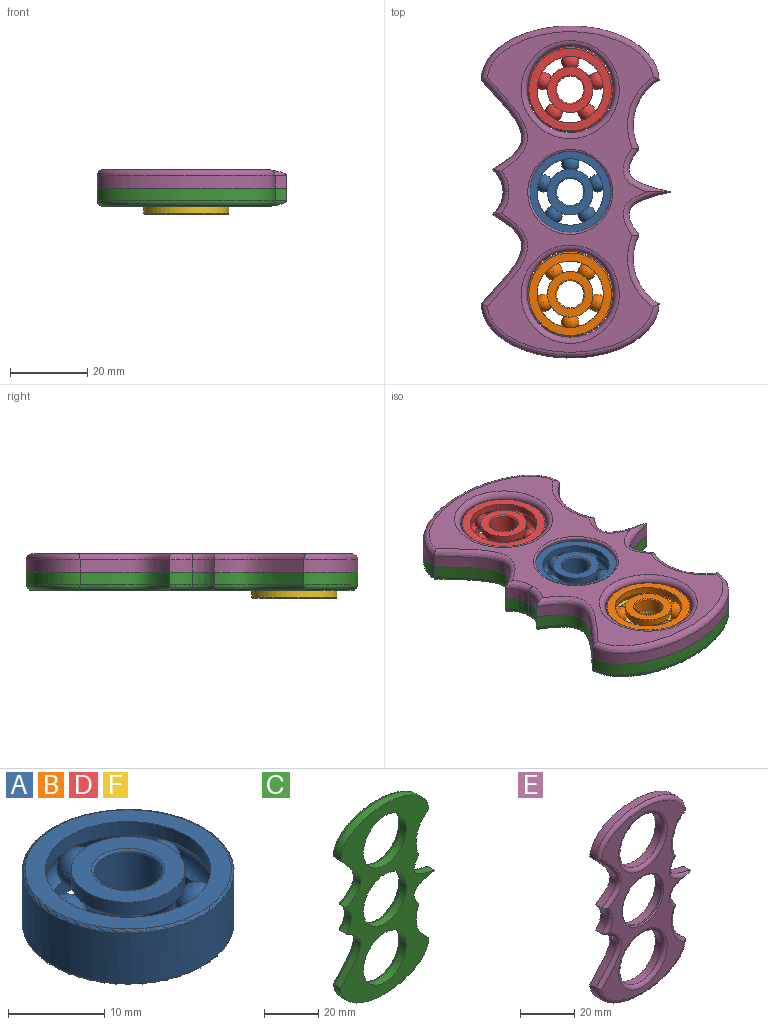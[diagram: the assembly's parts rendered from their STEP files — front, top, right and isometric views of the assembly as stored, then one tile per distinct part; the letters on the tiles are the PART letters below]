
ASSEMBLY  parts=6 mates=5
PART A: 29 faces, bbox 23.8x23.8x7 mm
  f0: torus R=3.8mm, axis (0,0,1), area 10.7mm2, adj f1,f2
  f1: cylinder r=3.5mm len=7mm, axis (0,0,1), area 140.7mm2, adj f0,f3
  f2: plane 11.8x11.8mm, normal (0,0,1), area 64mm2, adj f0,f14
  f3: torus R=3.8mm, axis (0,0,1), area 10.7mm2, adj f1,f4
  f4: plane 11.8x11.8mm, normal (0,0,-1), area 64mm2, adj f3,f25
  f5: torus R=10.7mm, axis (0,0,1), area 32.2mm2, adj f6,f7
  f6: cylinder r=11mm len=22mm, axis (0,0,1), area 442.3mm2, adj f5,f8
  f7: plane 21.4x21.4mm, normal (0,0,-1), area 127.3mm2, adj f5,f27
  f8: torus R=10.7mm, axis (0,0,1), area 32.2mm2, adj f6,f9
  f9: plane 21.4x21.4mm, normal (0,0,1), area 127.3mm2, adj f8,f19
  f10: sphere r=2.25mm, area 63.4mm2, adj f14,f15,f19,f23,f25,f26,f27,f28
  f11: sphere r=2.25mm, area 63.4mm2, adj f14,f18,f19,f22,f23,f25,f26,f27
  f12: sphere r=2.25mm, area 63.4mm2, adj f14,f17,f18,f19,f21,f22,f25,f27
  f13: sphere r=2.25mm, area 63.4mm2, adj f14,f16,f17,f19,f20,f21,f25,f27
  f14: cylinder r=5.9mm len=11.8mm, axis (0,0,1), area 63mm2, adj f2,f10,f11,f12,f13,f15,f16,f17
  f15: torus R=7.25mm, axis (0,0,1), area 27.7mm2, adj f10,f14,f24,f25
  f16: torus R=7.25mm, axis (0,0,1), area 27.7mm2, adj f13,f14,f24,f25
  f17: torus R=7.25mm, axis (0,0,1), area 27.7mm2, adj f12,f13,f14,f25
  f18: torus R=7.25mm, axis (0,0,1), area 27.7mm2, adj f11,f12,f14,f25
  f19: cylinder r=8.6mm len=17.2mm, axis (0,0,1), area 91.9mm2, adj f9,f10,f11,f12,f13,f20,f21,f22
  f20: torus R=7.25mm, axis (0,0,1), area 48.1mm2, adj f13,f19,f24,f27
  f21: torus R=7.25mm, axis (0,0,1), area 48.1mm2, adj f12,f13,f19,f27
  f22: torus R=7.25mm, axis (0,0,1), area 48.1mm2, adj f11,f12,f19,f27
  f23: torus R=7.25mm, axis (0,0,1), area 48.1mm2, adj f10,f11,f19,f27
  f24: sphere r=2.25mm, area 63.4mm2, adj f14,f15,f16,f19,f20,f25,f27,f28
  f25: cylinder r=5.9mm len=11.8mm, axis (0,0,1), area 63mm2, adj f4,f10,f11,f12,f13,f15,f16,f17
  f26: torus R=7.25mm, axis (0,0,1), area 27.7mm2, adj f10,f11,f14,f25
  f27: cylinder r=8.6mm len=17.2mm, axis (0,0,1), area 91.9mm2, adj f7,f10,f11,f12,f13,f20,f21,f22
  f28: torus R=7.25mm, axis (0,0,1), area 48.1mm2, adj f10,f19,f24,f27
PART B: same geometry as A
PART C: 28 faces, bbox 50.5x4.8x86 mm
  f0: extruded ~23.21x10.46mm, area 98.4mm2, adj f1,f12,f23,f27
  f1: extruded ~46x14mm, area 191.7mm2, adj f0,f2,f21,f27
  f2: cylinder r=13.62mm len=17.87mm, axis (0,1,0), area 66.6mm2, adj f1,f3,f19,f27
  f3: extruded ~11.13x10.77mm, area 61.8mm2, adj f2,f4,f17,f27
  f4: extruded ~11.13x10.77mm, area 61.8mm2, adj f3,f5,f18,f27
  f5: cylinder r=13.62mm len=17.87mm, axis (0,1,0), area 66.6mm2, adj f4,f6,f20,f27
  f6: extruded ~46x14mm, area 191.7mm2, adj f5,f7,f22,f27
  f7: extruded ~23.21x10.46mm, area 98.4mm2, adj f6,f8,f24,f27
  f8: extruded ~5.79x3.25mm, area 21.6mm2, adj f7,f12,f26,f27
  f9: cylinder r=11.2mm len=22.4mm, axis (0,1,0), area 228.7mm2, adj f16,f27
  f10: cylinder r=11.2mm len=22.4mm, axis (0,1,0), area 228.7mm2, adj f15,f27
  f11: cylinder r=11.2mm len=22.4mm, axis (0,1,0), area 228.7mm2, adj f14,f27
  f12: extruded ~5.79x3.25mm, area 21.6mm2, adj f0,f8,f25,f27
  f13: plane 83x42.94mm, normal (0,1,0), area 1082.8mm2, adj f14,f15,f16,f17,f18,f19,f20,f21
  f14: torus R=12.7mm, axis (0,-1,0), area 173.9mm2, adj f11,f13
  f15: torus R=12.7mm, axis (0,-1,0), area 173.9mm2, adj f10,f13
  f16: torus R=12.7mm, axis (0,-1,0), area 173.9mm2, adj f9,f13
  f17: bspline ~15.03x12.95mm, area 39.5mm2, adj f3,f13,f18,f19
  f18: bspline ~15.03x12.95mm, area 39.5mm2, adj f4,f13,f17,f20
  f19: torus R=15.12mm, axis (0,-1,0), area 48.1mm2, adj f2,f13,f17,f21
  f20: torus R=15.12mm, axis (0,-1,0), area 48.1mm2, adj f5,f13,f18,f22
  f21: bspline ~46.04x15.2mm, area 133.2mm2, adj f1,f13,f19,f23
  f22: bspline ~46.04x15.2mm, area 133.2mm2, adj f6,f13,f20,f24
  f23: bspline ~26.86x12.79mm, area 70.7mm2, adj f0,f13,f21,f25
  f24: bspline ~26.86x12.79mm, area 70.7mm2, adj f7,f13,f22,f26
  f25: bspline ~8.37x5.47mm, area 14.6mm2, adj f12,f13,f23,f26
  f26: bspline ~9.72x5.47mm, area 14.6mm2, adj f8,f13,f24,f25
  f27: plane 86x49mm, normal (0,-1,0), area 1811.4mm2, adj f0,f1,f2,f3,f4,f5,f6,f7
PART D: same geometry as A
PART E: 30 faces, bbox 50.5x4.8x86 mm
  f0: cylinder r=11.2mm len=22.4mm, axis (0,1,0), area 263.9mm2, adj f14,f16
  f1: cylinder r=11.2mm len=22.4mm, axis (0,1,0), area 228.7mm2, adj f14,f19
  f2: cylinder r=11.2mm len=22.4mm, axis (0,1,0), area 228.7mm2, adj f14,f18
  f3: plane 83x42.94mm, normal (0,-1,0), area 1209.4mm2, adj f17,f18,f19,f20,f21,f22,f23,f24
  f4: extruded ~5.79x3.25mm, area 21.6mm2, adj f5,f13,f14,f28
  f5: extruded ~5.79x3.25mm, area 21.6mm2, adj f4,f6,f14,f29
  f6: extruded ~23.21x10.46mm, area 98.4mm2, adj f5,f7,f14,f27
  f7: extruded ~46x14mm, area 191.7mm2, adj f6,f8,f14,f25
  f8: cylinder r=13.62mm len=17.87mm, axis (0,1,0), area 66.6mm2, adj f7,f9,f14,f23
  f9: extruded ~11.13x10.77mm, area 61.8mm2, adj f8,f10,f14,f21
  f10: extruded ~11.13x10.77mm, area 61.8mm2, adj f9,f11,f14,f20
  f11: cylinder r=13.62mm len=17.87mm, axis (0,1,0), area 66.6mm2, adj f10,f12,f14,f22
  f12: extruded ~46x14mm, area 191.7mm2, adj f11,f13,f14,f24
  f13: extruded ~23.21x10.46mm, area 98.4mm2, adj f4,f12,f14,f26
  f14: plane 86x49mm, normal (0,1,0), area 1811.4mm2, adj f0,f1,f2,f4,f5,f6,f7,f8
  f15: cylinder r=10.5mm len=21mm, axis (0,-1,0), area 33mm2, adj f16,f17
  f16: plane 22.4x22.4mm, normal (0,1,0), area 47.7mm2, adj f0,f15
  f17: torus R=11mm, axis (0,-1,0), area 52.7mm2, adj f3,f15
  f18: torus R=12.7mm, axis (0,-1,0), area 173.9mm2, adj f2,f3
  f19: torus R=12.7mm, axis (0,-1,0), area 173.9mm2, adj f1,f3
  f20: bspline ~15.03x12.95mm, area 39.5mm2, adj f3,f10,f21,f22
  f21: bspline ~15.03x12.95mm, area 39.5mm2, adj f3,f9,f20,f23
  f22: torus R=15.12mm, axis (0,-1,0), area 48.1mm2, adj f3,f11,f20,f24
  f23: torus R=15.12mm, axis (0,-1,0), area 48.1mm2, adj f3,f8,f21,f25
  f24: bspline ~46.04x15.2mm, area 133.2mm2, adj f3,f12,f22,f26
  f25: bspline ~46.04x15.2mm, area 133.2mm2, adj f3,f7,f23,f27
  f26: bspline ~26.86x12.79mm, area 70.7mm2, adj f3,f13,f24,f28
  f27: bspline ~26.86x12.79mm, area 70.7mm2, adj f3,f6,f25,f29
  f28: bspline ~8.37x5.47mm, area 14.6mm2, adj f3,f4,f26,f29
  f29: bspline ~9.72x5.47mm, area 14.6mm2, adj f3,f5,f27,f28
PART F: same geometry as A
PLACE A at identity fixed
PLACE B rot(axis=(1,0,0),180deg) t=(0,-26.5,7)mm
PLACE C rot(axis=(-1,0,0),90deg) t=(0,0,3.5)mm
PLACE D t=(0,26.5,0)mm
PLACE E rot(axis=(-1,0,0),90deg) t=(0,0,3.5)mm
PLACE F rot(axis=(1,0,0),180deg) t=(0,-26.5,3.75)mm
MATE fastened F.f0 <-> C.f10  axis (0,0,-1) through (0,-26.5,0.25)mm
MATE fastened D.f0 <-> E.f2  axis (0,0,1) through (0,26.5,3.5)mm
MATE revolute E.f0 <-> A.f0  axis (0,0,-1) through (0,0,3.5)mm
MATE revolute C.f9 <-> A.f0  axis (0,0,1) through (0,0,3.5)mm
MATE fastened B.f0 <-> C.f10  axis (0,0,-1) through (0,-26.5,3.5)mm
